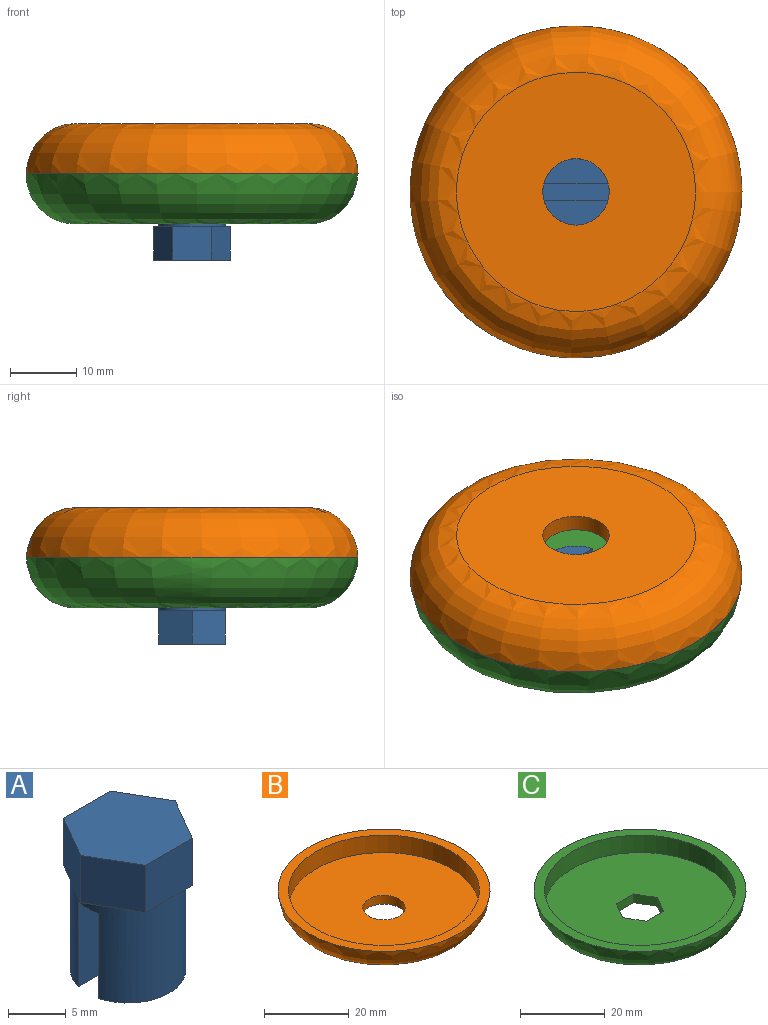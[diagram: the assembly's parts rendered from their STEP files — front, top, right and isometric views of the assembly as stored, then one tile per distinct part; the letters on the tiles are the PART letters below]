
ASSEMBLY  parts=3 mates=2
PART A: 19 faces, bbox 11.5x10x15 mm
  f0: plane 9.68x3.75mm, normal (0,0,-1), area 26.9mm2, adj f2,f16
  f1: plane 9.68x3.75mm, normal (0,0,-1), area 26.9mm2, adj f2,f17
  f2: cylinder r=5mm len=10mm, axis (0,0,-1), area 268.7mm2, adj f0,f1,f3,f4,f5,f6,f7,f8
  f3: plane 4.33x2.5mm, normal (0,0,-1), area 1.3mm2, adj f2,f11,f12
  f4: plane 4.33x2.5mm, normal (0,0,-1), area 1.3mm2, adj f2,f12,f13
  f5: plane 5x1.44mm, normal (0,0,-1), area 1.3mm2, adj f2,f13,f14
  f6: plane 4.33x2.5mm, normal (0,0,-1), area 1.3mm2, adj f2,f9,f14
  f7: plane 4.33x2.5mm, normal (0,0,-1), area 1.3mm2, adj f2,f9,f10
  f8: plane 5x1.44mm, normal (0,0,-1), area 1.3mm2, adj f2,f10,f11
  f9: plane 5.77x5mm, normal (0,-1,0), area 28.9mm2, adj f6,f7,f10,f14,f15
  f10: plane 5x5mm, normal (0.87,-0.5,0), area 28.9mm2, adj f7,f8,f9,f11,f15
  f11: plane 5x5mm, normal (0.87,0.5,0), area 28.9mm2, adj f3,f8,f10,f12,f15
  f12: plane 5.77x5mm, normal (0,1,0), area 28.9mm2, adj f3,f4,f11,f13,f15
  f13: plane 5x5mm, normal (-0.87,0.5,0), area 28.9mm2, adj f4,f5,f12,f14,f15
  f14: plane 5x5mm, normal (-0.87,-0.5,0), area 28.9mm2, adj f5,f6,f9,f13,f15
  f15: plane 11.55x10mm, normal (0,0,1), area 86.6mm2, adj f9,f10,f11,f12,f13,f14
  f16: plane 9.68x9mm, normal (0,1,0), area 87.1mm2, adj f0,f2,f18
  f17: plane 9.68x9mm, normal (0,-1,0), area 87.1mm2, adj f1,f2,f18
  f18: plane 10x2.5mm, normal (0,0,-1), area 24.7mm2, adj f2,f16,f17
PART B: 6 faces, bbox 50x50x7.5 mm
  f0: plane 36x36mm, normal (0,0,-1), area 939.3mm2, adj f2,f5
  f1: plane 50x50mm, normal (0,0,1), area 373.1mm2, adj f2,f3
  f2: revolved ~50x50mm, area 1600.6mm2, adj f0,f1
  f3: cylinder r=22.5mm len=45mm, axis (0,0,1), area 706.9mm2, adj f1,f4
  f4: plane 45x45mm, normal (0,0,1), area 1511.9mm2, adj f3,f5
  f5: cylinder r=5mm len=10mm, axis (0,0,1), area 78.5mm2, adj f0,f4
PART C: 11 faces, bbox 50x50x7.5 mm
  f0: plane 36x36mm, normal (0,0,-1), area 931.3mm2, adj f2,f5,f6,f7,f8,f9,f10
  f1: plane 50x50mm, normal (0,0,1), area 373.1mm2, adj f2,f3
  f2: revolved ~50x50mm, area 1600.6mm2, adj f0,f1
  f3: cylinder r=22.5mm len=45mm, axis (0,0,1), area 706.9mm2, adj f1,f4
  f4: plane 45x45mm, normal (0,0,1), area 1503.8mm2, adj f3,f5,f6,f7,f8,f9,f10
  f5: plane 5.77x2.5mm, normal (0,1,0), area 14.4mm2, adj f0,f4,f6,f10
  f6: plane 5x2.89mm, normal (-0.87,0.5,0), area 14.4mm2, adj f0,f4,f5,f7
  f7: plane 5x2.89mm, normal (-0.87,-0.5,0), area 14.4mm2, adj f0,f4,f6,f8
  f8: plane 5.77x2.5mm, normal (0,-1,0), area 14.4mm2, adj f0,f4,f7,f9
  f9: plane 5x2.89mm, normal (0.87,-0.5,0), area 14.4mm2, adj f0,f4,f8,f10
  f10: plane 5x2.89mm, normal (0.87,0.5,0), area 14.4mm2, adj f0,f4,f5,f9
PLACE A rot(axis=(0,-1,0),180deg) t=(-18.06,-36.12,13.61)mm
PLACE B rot(axis=(0,-1,0),180deg) t=(-18.06,-36.12,19.11)mm
PLACE C t=(-18.06,-36.12,4.11)mm
MATE slider A.f2 <-> B.f5  axis (0,0,-1) through (-18.06,-36.12,-1.39)mm
MATE fastened C.f3 <-> B.f5  axis (0,0,-1) through (-18.06,-36.12,6.36)mm
